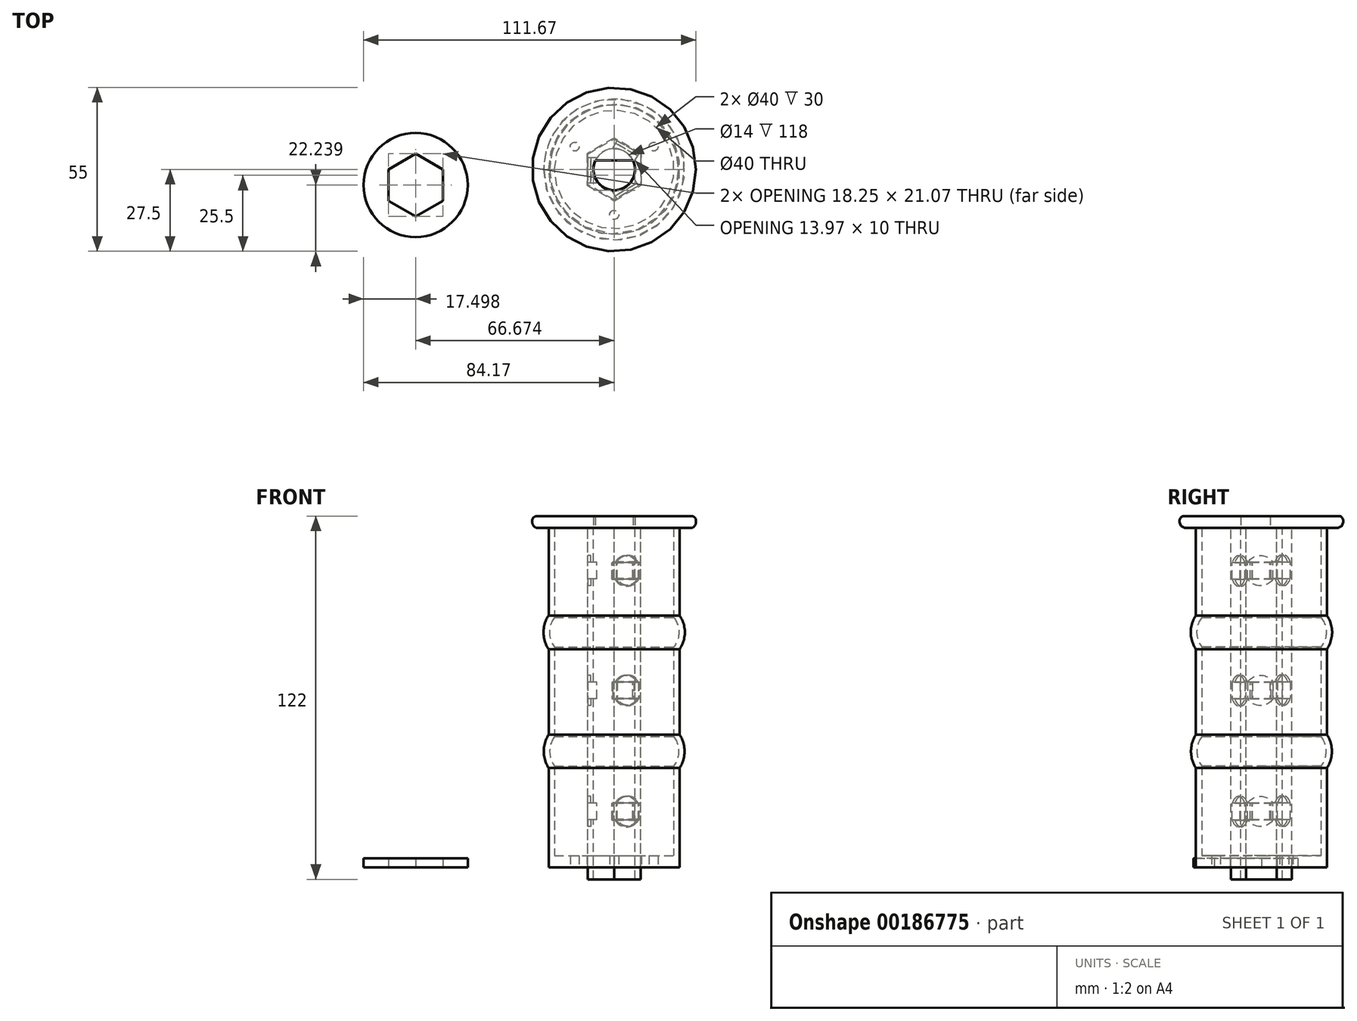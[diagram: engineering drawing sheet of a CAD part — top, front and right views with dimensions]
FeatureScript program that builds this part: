
annotation { "Feature Type Name" : "Feature", "Feature Type Description" : "" }
export const myFeature = defineFeature(function(context is Context, id is Id, definition is map)
    precondition{}
    {
        {
            var Q0;
            Q0=qCreatedBy(makeId("Front.planeOp"),FACE);
            var sketch = newSketch(context, id + "F0", { "sketchPlane" : qUnion([Q0])});
            skLineSegment(sketch, "E0.bottom", {"start": v(-20, 0) * mm, "end": v(20, 0) * mm});
            skLineSegment(sketch, "E0.top", {"start": v(-20, 4) * mm, "end": v(20, 4) * mm});
            skLineSegment(sketch, "E0.left", {"start": v(-20, 0) * mm, "end": v(-20, 4) * mm});
            skLineSegment(sketch, "E0.right", {"start": v(20, 0) * mm, "end": v(20, 4) * mm});
            skLineSegment(sketch, "E1.top", {"start": v(-20, 34) * mm, "end": v(20, 34) * mm});
            skLineSegment(sketch, "E1.left", {"start": v(-20, 4) * mm, "end": v(-20, 34) * mm});
            skLineSegment(sketch, "E1.right", {"start": v(20, 4) * mm, "end": v(20, 34) * mm});
            skLineSegment(sketch, "E2.top", {"start": v(-20, 44) * mm, "end": v(20, 44) * mm});
            skLineSegment(sketch, "E2.left", {"start": v(-20, 34) * mm, "end": v(-20, 44) * mm});
            skLineSegment(sketch, "E2.right", {"start": v(20, 34) * mm, "end": v(20, 44) * mm});
            skLineSegment(sketch, "E3", {"start": v(0, 0) * mm, "end": v(0, 48) * mm});
            skLineSegment(sketch, "E4.bottom", {"start": v(0, 0) * mm, "end": v(7, 0) * mm});
            skLineSegment(sketch, "E4.top", {"start": v(0, 4) * mm, "end": v(7, 4) * mm});
            skLineSegment(sketch, "E4.left", {"start": v(0, 0) * mm, "end": v(0, 4) * mm});
            skLineSegment(sketch, "E4.right", {"start": v(7, 0) * mm, "end": v(7, 4) * mm});
            skLineSegment(sketch, "E5.top", {"start": v(-20, 74) * mm, "end": v(20, 74) * mm});
            skLineSegment(sketch, "E5.left", {"start": v(-20, 44) * mm, "end": v(-20, 74) * mm});
            skLineSegment(sketch, "E5.right", {"start": v(20, 44) * mm, "end": v(20, 74) * mm});
            skLineSegment(sketch, "E6.top", {"start": v(-20, 84) * mm, "end": v(20, 84) * mm});
            skLineSegment(sketch, "E6.left", {"start": v(-20, 74) * mm, "end": v(-20, 84) * mm});
            skLineSegment(sketch, "E6.right", {"start": v(20, 74) * mm, "end": v(20, 84) * mm});
            skLineSegment(sketch, "E7.top", {"start": v(-20, 114) * mm, "end": v(20, 114) * mm});
            skLineSegment(sketch, "E7.left", {"start": v(-20, 84) * mm, "end": v(-20, 114) * mm});
            skLineSegment(sketch, "E7.right", {"start": v(20, 84) * mm, "end": v(20, 114) * mm});
            skPoint(sketch, "E8.third.point", {"position": v(0, 39) * mm});
            skPoint(sketch, "E8.third.point.positionSnap0", {"position": v(20, 39) * mm});
            skPoint(sketch, "E9.third.point", {"position": v(0, 79) * mm});
            skPoint(sketch, "E9.third.point.positionSnap0", {"position": v(20, 79) * mm});
            skArc(sketch, "E10", {"start": v(20, 34) * mm, "mid": v(21.65, 39) * mm, "end": v(20, 44) * mm});
            skArc(sketch, "E11", {"start": v(20, 74) * mm, "mid": v(21.75, 79) * mm, "end": v(20, 84) * mm});
            skLineSegment(sketch, "E12.0", {"start": v(22, 84.66) * mm, "end": v(22, 114) * mm});
            skArc(sketch, "E12.1", {"start": v(22, 73.34) * mm, "mid": v(23.75, 79) * mm, "end": v(22, 84.66) * mm});
            skLineSegment(sketch, "E12.2", {"start": v(22, 0) * mm, "end": v(22, 4) * mm});
            skLineSegment(sketch, "E12.3", {"start": v(22, 4) * mm, "end": v(22, 33.38) * mm});
            skArc(sketch, "E12.4", {"start": v(22, 33.38) * mm, "mid": v(23.65, 39) * mm, "end": v(22, 44.62) * mm});
            skLineSegment(sketch, "E12.5", {"start": v(22, 44.62) * mm, "end": v(22, 73.34) * mm});
            skLineSegment(sketch, "E13", {"start": v(20, 0) * mm, "end": v(22, 0) * mm});
            skLineSegment(sketch, "E14", {"start": v(20, 114) * mm, "end": v(22, 114) * mm});
            skPoint(sketch, "E15.visualSharp", {"position": v(22, 114) * mm});
            skLineSegment(sketch, "E15.filletArc", {"start": v(22, 114) * mm, "end": v(22, 114) * mm});
            skPoint(sketch, "E16.visualSharp", {"position": v(20, 114) * mm});
            skLineSegment(sketch, "E16.filletArc", {"start": v(20, 114) * mm, "end": v(20, 114) * mm});
            skSolve(sketch);
        }
        {
            var Q0;
            Q0=makeQuery(id+"F0.imprint","IMPRINT",FACE,{"disambiguationData":[TD([[makeQuery(id+"F0.imprint","IMPRINT",EDGE,{"derivedFrom":sQuery(id+"F0.wireOp",EDGE,"E0.right")}),-1.0]])]});
            var Q1;
            {var subQ0=sQuery(id+"F0.wireOp",EDGE,"E0.right");Q1=makeQuery(id+"F0.imprint","IMPRINT",FACE,{"disambiguationData":[TD([[makeQuery(id+"F0.imprint","IMPRINT",EDGE,{"derivedFrom":subQ0}),1.0]])]});}
            var Q2;
            Q2=sQuery(id+"F0.wireOp",EDGE,"E3");
            revolve(context, id + "F1", {"entities" : qUnion([Q0, Q1]), "axis" : qUnion([Q2]), "revolveType" : RevolveType.FULL});
        }
        {
            var Q0;
            Q0=makeQuery(id+"F1.opRevolve","SWEPT_FACE",FACE,{"disambiguationData":[OSD([sQuery(id+"F0.wireOp",EDGE,"E0.bottom"),sQuery(id+"F0.wireOp",EDGE,"E13")])]});
            var sketch = newSketch(context, id + "F2", { "sketchPlane" : qUnion([Q0])});
            skCircle(sketch, "E17.cCircle", {"center": v(0, 0) * mm, "radius": 13.23 * mm, "construction": true});
            skLineSegment(sketch, "E17.0", {"start": v(0, 15.28) * mm, "end": v(13.23, 7.64) * mm});
            skLineSegment(sketch, "E17.1", {"start": v(13.23, 7.64) * mm, "end": v(13.23, -7.64) * mm});
            skLineSegment(sketch, "E17.2", {"start": v(13.23, -7.64) * mm, "end": v(0, -15.28) * mm});
            skLineSegment(sketch, "E17.3", {"start": v(0, -15.28) * mm, "end": v(-13.23, -7.64) * mm});
            skLineSegment(sketch, "E17.4", {"start": v(-13.23, -7.64) * mm, "end": v(-13.23, 7.64) * mm});
            skLineSegment(sketch, "E17.5", {"start": v(-13.23, 7.64) * mm, "end": v(0, 15.28) * mm});
            skPoint(sketch, "E17.0.midPoint", {"position": v(6.61, 11.46) * mm});
            skCircle(sketch, "E18", {"center": v(0, 15.28) * mm, "radius": 1.5 * mm});
            skCircle(sketch, "E19", {"center": v(-13.23, -7.64) * mm, "radius": 1.5 * mm});
            skCircle(sketch, "E20", {"center": v(13.23, -7.64) * mm, "radius": 1.5 * mm});
            skCircle(sketch, "E21.cCircle", {"center": v(0, 0) * mm, "radius": 8.88 * mm, "construction": true});
            skLineSegment(sketch, "E21.0", {"start": v(8.88, 5.12) * mm, "end": v(8.88, -5.12) * mm});
            skLineSegment(sketch, "E21.1", {"start": v(8.88, -5.12) * mm, "end": v(0, -10.25) * mm});
            skLineSegment(sketch, "E21.2", {"start": v(0, -10.25) * mm, "end": v(-8.87, -5.12) * mm});
            skLineSegment(sketch, "E21.3", {"start": v(-8.87, -5.12) * mm, "end": v(-8.87, 5.12) * mm});
            skLineSegment(sketch, "E21.4", {"start": v(-8.87, 5.12) * mm, "end": v(0, 10.25) * mm});
            skLineSegment(sketch, "E21.5", {"start": v(0, 10.25) * mm, "end": v(8.88, 5.12) * mm});
            skPoint(sketch, "E21.0.midPoint", {"position": v(8.88, 0) * mm});
            skCircle(sketch, "E22", {"center": v(0, 0) * mm, "radius": 7 * mm});
            skCircle(sketch, "E23.cCircle", {"center": v(0, 0) * mm, "radius": 8.47 * mm, "construction": true});
            skLineSegment(sketch, "E23.0", {"start": v(0, 9.78) * mm, "end": v(8.47, 4.89) * mm});
            skLineSegment(sketch, "E23.1", {"start": v(8.47, 4.89) * mm, "end": v(8.47, -4.89) * mm});
            skLineSegment(sketch, "E23.2", {"start": v(8.47, -4.89) * mm, "end": v(0, -9.78) * mm});
            skLineSegment(sketch, "E23.3", {"start": v(0, -9.78) * mm, "end": v(-8.47, -4.89) * mm});
            skLineSegment(sketch, "E23.4", {"start": v(-8.47, -4.89) * mm, "end": v(-8.47, 4.89) * mm});
            skLineSegment(sketch, "E23.5", {"start": v(-8.47, 4.89) * mm, "end": v(0, 9.78) * mm});
            skPoint(sketch, "E23.0.midPoint", {"position": v(4.24, 7.33) * mm});
            skCircle(sketch, "E24.cCircle", {"center": v(0, 0) * mm, "radius": 9.12 * mm, "construction": true});
            skLineSegment(sketch, "E24.0", {"start": v(0, 10.54) * mm, "end": v(9.13, 5.27) * mm});
            skLineSegment(sketch, "E24.1", {"start": v(9.13, 5.27) * mm, "end": v(9.13, -5.27) * mm});
            skLineSegment(sketch, "E24.2", {"start": v(9.13, -5.27) * mm, "end": v(0, -10.54) * mm});
            skLineSegment(sketch, "E24.3", {"start": v(0, -10.54) * mm, "end": v(-9.12, -5.27) * mm});
            skLineSegment(sketch, "E24.4", {"start": v(-9.12, -5.27) * mm, "end": v(-9.12, 5.27) * mm});
            skLineSegment(sketch, "E24.5", {"start": v(-9.12, 5.27) * mm, "end": v(0, 10.54) * mm});
            skPoint(sketch, "E24.0.midPoint", {"position": v(4.57, 7.9) * mm});
            skSolve(sketch);
        }
        {
            var Q0;
            {var subQ0=sQuery(id+"F2.wireOp",EDGE,"E17.5");var subQ1=sQuery(id+"F2.wireOp",EDGE,"E17.0");var subQ2=makeQuery(id+"F2.imprint","INTERSECT",VERTEX,{"derivedFrom":[subQ1,subQ0]});Q0=makeQuery(id+"F2.imprint","IMPRINT",FACE,{"disambiguationData":[TD([[makeQuery(id+"F2.imprint","IMPRINT",EDGE,{"disambiguationData":[TD([[subQ2,-1.0]])],"derivedFrom":subQ1}),-1.0]])]});}
            var Q1;
            {var subQ0=sQuery(id+"F2.wireOp",EDGE,"E17.5");var subQ1=sQuery(id+"F2.wireOp",EDGE,"E17.0");var subQ2=makeQuery(id+"F2.imprint","INTERSECT",VERTEX,{"derivedFrom":[subQ1,subQ0]});Q1=makeQuery(id+"F2.imprint","IMPRINT",FACE,{"disambiguationData":[TD([[makeQuery(id+"F2.imprint","IMPRINT",EDGE,{"disambiguationData":[TD([[subQ2,-1.0]])],"derivedFrom":subQ1}),1.0]])]});}
            var Q2;
            {var subQ0=sQuery(id+"F2.wireOp",EDGE,"E17.2");var subQ1=sQuery(id+"F2.wireOp",EDGE,"E17.1");var subQ2=makeQuery(id+"F2.imprint","INTERSECT",VERTEX,{"derivedFrom":[subQ1,subQ0]});Q2=makeQuery(id+"F2.imprint","IMPRINT",FACE,{"disambiguationData":[TD([[makeQuery(id+"F2.imprint","IMPRINT",EDGE,{"disambiguationData":[TD([[subQ2,1.0]])],"derivedFrom":subQ1}),1.0]])]});}
            var Q3;
            {var subQ0=sQuery(id+"F2.wireOp",EDGE,"E17.2");var subQ1=sQuery(id+"F2.wireOp",EDGE,"E17.1");var subQ2=makeQuery(id+"F2.imprint","INTERSECT",VERTEX,{"derivedFrom":[subQ1,subQ0]});Q3=makeQuery(id+"F2.imprint","IMPRINT",FACE,{"disambiguationData":[TD([[makeQuery(id+"F2.imprint","IMPRINT",EDGE,{"disambiguationData":[TD([[subQ2,1.0]])],"derivedFrom":subQ1}),-1.0]])]});}
            var Q4;
            {var subQ0=sQuery(id+"F2.wireOp",EDGE,"E17.4");var subQ1=sQuery(id+"F2.wireOp",EDGE,"E17.3");var subQ2=makeQuery(id+"F2.imprint","INTERSECT",VERTEX,{"derivedFrom":[subQ1,subQ0]});Q4=makeQuery(id+"F2.imprint","IMPRINT",FACE,{"disambiguationData":[TD([[makeQuery(id+"F2.imprint","IMPRINT",EDGE,{"disambiguationData":[TD([[subQ2,1.0]])],"derivedFrom":subQ1}),-1.0]])]});}
            var Q5;
            {var subQ0=sQuery(id+"F2.wireOp",EDGE,"E17.4");var subQ1=sQuery(id+"F2.wireOp",EDGE,"E17.3");var subQ2=makeQuery(id+"F2.imprint","INTERSECT",VERTEX,{"derivedFrom":[subQ1,subQ0]});Q5=makeQuery(id+"F2.imprint","IMPRINT",FACE,{"disambiguationData":[TD([[makeQuery(id+"F2.imprint","IMPRINT",EDGE,{"disambiguationData":[TD([[subQ2,1.0]])],"derivedFrom":subQ1}),1.0]])]});}
            var Q6;
            Q6=makeQuery(id+"F2.imprint","IMPRINT",FACE,{"disambiguationData":[TD([[makeQuery(id+"F2.imprint","IMPRINT",EDGE,{"derivedFrom":sQuery(id+"F2.wireOp",EDGE,"E23.0")}),-1.0]])]});
            var Q7;
            Q7=makeQuery(id+"F2.imprint","IMPRINT",FACE,{"disambiguationData":[TD([[makeQuery(id+"F2.imprint","IMPRINT",EDGE,{"derivedFrom":sQuery(id+"F2.wireOp",EDGE,"E21.0")}),-1.0]])]});
            var Q8;
            Q8=makeQuery(id+"F2.imprint","IMPRINT",FACE,{"disambiguationData":[TD([[makeQuery(id+"F2.imprint","IMPRINT",EDGE,{"derivedFrom":sQuery(id+"F2.wireOp",EDGE,"E21.0")}),1.0]])]});
            extrude(context, id + "F3", {"entities" : qUnion([Q0, Q1, Q2, Q3, Q4, Q5, Q6, Q7, Q8]), "operationType" : NewBodyOperationType.REMOVE, "oppositeDirection" : true, "depth" : 4 * mm});
        }
        {
            var Q0;
            Q0=makeQuery(id+"F1.opRevolve","SWEPT_FACE",FACE,{"disambiguationData":[OSD([sQuery(id+"F0.wireOp",EDGE,"E14")])]});
            var sketch = newSketch(context, id + "F4", { "sketchPlane" : qUnion([Q0])});
            skCircle(sketch, "E25.cCircle", {"center": v(0, 0) * mm, "radius": 8.88 * mm, "construction": true});
            skLineSegment(sketch, "E25.0", {"start": v(8.88, 5.12) * mm, "end": v(8.88, -5.12) * mm});
            skLineSegment(sketch, "E25.1", {"start": v(8.88, -5.12) * mm, "end": v(0, -10.25) * mm});
            skLineSegment(sketch, "E25.2", {"start": v(0, -10.25) * mm, "end": v(-8.88, -5.12) * mm});
            skLineSegment(sketch, "E25.3", {"start": v(-8.88, -5.12) * mm, "end": v(-8.88, 5.12) * mm});
            skLineSegment(sketch, "E25.4", {"start": v(-8.88, 5.12) * mm, "end": v(0, 10.25) * mm});
            skLineSegment(sketch, "E25.5", {"start": v(0, 10.25) * mm, "end": v(8.88, 5.12) * mm});
            skPoint(sketch, "E25.0.midPoint", {"position": v(8.88, 0) * mm});
            skCircle(sketch, "E26", {"center": v(0, 0) * mm, "radius": 7 * mm});
            skCircle(sketch, "E27", {"center": v(0, 0) * mm, "radius": 27.5 * mm});
            skLineSegment(sketch, "E28", {"start": v(0, 3) * mm, "end": v(6.32, 3) * mm});
            skLineSegment(sketch, "E29", {"start": v(0, 3) * mm, "end": v(-6.32, 3) * mm});
            skSolve(sketch);
        }
        {
            var Q0;
            Q0=makeQuery(id+"F4.imprint","IMPRINT",FACE,{"disambiguationData":[TD([[makeQuery(id+"F4.imprint","IMPRINT",EDGE,{"derivedFrom":sQuery(id+"F4.wireOp",EDGE,"E25.0")}),-1.0]])]});
            extrude(context, id + "F5", {"entities" : qUnion([Q0]), "oppositeDirection" : true, "depth" : 118 * mm});
        }
        {
            var Q0;
            Q0=makeQuery(id+"F4.imprint","IMPRINT",FACE,{"disambiguationData":[TD([[makeQuery(id+"F4.imprint","IMPRINT",EDGE,{"derivedFrom":sQuery(id+"F4.wireOp",EDGE,"E27")}),1.0]])]});
            var Q1;
            {var subQ0=sQuery(id+"F0.wireOp",EDGE,"E14");Q1=makeQuery(id+"F4.imprint","IMPRINT",FACE,{"disambiguationData":[TD([[makeQuery(id+"F4.imprint","IMPRINT",EDGE,{"derivedFrom":makeQuery(id+"F1.opRevolve","SWEPT_EDGE",EDGE,{"disambiguationData":[OSD([subQ0,sQuery(id+"F0.wireOp",EDGE,"E16.filletArc")])]})}),1.0]])]});}
            var Q2;
            Q2=makeQuery(id+"F4.imprint","IMPRINT",FACE,{"disambiguationData":[TD([[makeQuery(id+"F4.imprint","IMPRINT",EDGE,{"derivedFrom":sQuery(id+"F4.wireOp",EDGE,"E25.0")}),1.0]])]});
            var Q3;
            Q3=makeQuery(id+"F4.imprint","IMPRINT",FACE,{"disambiguationData":[TD([[makeQuery(id+"F4.imprint","IMPRINT",EDGE,{"derivedFrom":sQuery(id+"F4.wireOp",EDGE,"E25.0")}),-1.0]])]});
            var Q4;
            {var subQ0=sQuery(id+"F0.wireOp",EDGE,"E14");Q4=makeQuery(id+"F4.imprint","IMPRINT",FACE,{"disambiguationData":[TD([[makeQuery(id+"F4.imprint","IMPRINT",EDGE,{"derivedFrom":makeQuery(id+"F1.opRevolve","SWEPT_EDGE",EDGE,{"disambiguationData":[OSD([sQuery(id+"F0.wireOp",EDGE,"E12.0"),subQ0])]})}),-1.0]])]});}
            var Q5;
            {var subQ0=sQuery(id+"F4.wireOp",EDGE,"E28");Q5=makeQuery(id+"F4.imprint","IMPRINT",FACE,{"disambiguationData":[TD([[makeQuery(id+"F4.imprint","IMPRINT",EDGE,{"derivedFrom":subQ0}),1.0]])]});}
            extrude(context, id + "F6", {"entities" : qUnion([Q0, Q1, Q2, Q3, Q4, Q5]), "depth" : 4 * mm});
        }
        {
            var Q0;
            Q0=makeQuery(id+"F6.opExtrude","CAP_EDGE",EDGE,{"disambiguationData":[OSD([sQuery(id+"F4.wireOp",EDGE,"E27")])],"isStart":true});
            fillet(context, id + "F7", {"entities" : qUnion([Q0]), "radius" : 2 * mm, "tangentPropagation" : true, "allowEdgeOverflow" : false});
        }
        {
            var Q0;
            Q0=makeQuery(id+"F5.opExtrude","SWEPT_FACE",FACE,{"disambiguationData":[OSD([sQuery(id+"F4.wireOp",EDGE,"E25.1")])]});
            var sketch = newSketch(context, id + "F8", { "sketchPlane" : qUnion([Q0])});
            skCircle(sketch, "E30", {"center": v(0, 59.42) * mm, "radius": 5.1 * mm});
            skPoint(sketch, "E30.centerSnap0", {"position": v(0, 114) * mm});
            skCircle(sketch, "E31", {"center": v(0, 99.62) * mm, "radius": 5.1 * mm});
            skCircle(sketch, "E32", {"center": v(0, 18.73) * mm, "radius": 5.1 * mm});
            skLineSegment(sketch, "E33.bottom", {"start": v(-4.25, 62.24) * mm, "end": v(4.25, 62.24) * mm});
            skLineSegment(sketch, "E33.top", {"start": v(-4.25, 56.6) * mm, "end": v(4.25, 56.6) * mm});
            skLineSegment(sketch, "E33.left", {"start": v(-4.25, 62.24) * mm, "end": v(-4.25, 56.6) * mm});
            skLineSegment(sketch, "E33.right", {"start": v(4.25, 62.24) * mm, "end": v(4.25, 56.6) * mm});
            skLineSegment(sketch, "E34.bottom", {"start": v(-4.25, 96.8) * mm, "end": v(4.25, 96.8) * mm});
            skLineSegment(sketch, "E34.top", {"start": v(-4.25, 102.44) * mm, "end": v(4.25, 102.44) * mm});
            skLineSegment(sketch, "E34.left", {"start": v(-4.25, 96.8) * mm, "end": v(-4.25, 102.44) * mm});
            skLineSegment(sketch, "E34.right", {"start": v(4.25, 96.8) * mm, "end": v(4.25, 102.44) * mm});
            skLineSegment(sketch, "E35.bottom", {"start": v(-4.25, 15.91) * mm, "end": v(4.25, 15.91) * mm});
            skLineSegment(sketch, "E35.top", {"start": v(-4.25, 21.55) * mm, "end": v(4.25, 21.55) * mm});
            skLineSegment(sketch, "E35.left", {"start": v(-4.25, 15.91) * mm, "end": v(-4.25, 21.55) * mm});
            skLineSegment(sketch, "E35.right", {"start": v(4.25, 15.91) * mm, "end": v(4.25, 21.55) * mm});
            skSolve(sketch);
        }
        {
            var Q0;
            {var subQ0=sQuery(id+"F8.wireOp",EDGE,"E33.bottom");Q0=makeQuery(id+"F8.imprint","IMPRINT",FACE,{"disambiguationData":[TD([[makeQuery(id+"F8.imprint","IMPRINT",EDGE,{"derivedFrom":subQ0}),1.0]])]});}
            var Q1;
            {var subQ0=sQuery(id+"F8.wireOp",EDGE,"E33.top");Q1=makeQuery(id+"F8.imprint","IMPRINT",FACE,{"disambiguationData":[TD([[makeQuery(id+"F8.imprint","IMPRINT",EDGE,{"derivedFrom":subQ0}),-1.0]])]});}
            var Q2;
            {var subQ0=sQuery(id+"F8.wireOp",EDGE,"E34.top");Q2=makeQuery(id+"F8.imprint","IMPRINT",FACE,{"disambiguationData":[TD([[makeQuery(id+"F8.imprint","IMPRINT",EDGE,{"derivedFrom":subQ0}),1.0]])]});}
            var Q3;
            {var subQ0=sQuery(id+"F8.wireOp",EDGE,"E34.bottom");Q3=makeQuery(id+"F8.imprint","IMPRINT",FACE,{"disambiguationData":[TD([[makeQuery(id+"F8.imprint","IMPRINT",EDGE,{"derivedFrom":subQ0}),-1.0]])]});}
            var Q4;
            {var subQ0=sQuery(id+"F8.wireOp",EDGE,"E35.top");Q4=makeQuery(id+"F8.imprint","IMPRINT",FACE,{"disambiguationData":[TD([[makeQuery(id+"F8.imprint","IMPRINT",EDGE,{"derivedFrom":subQ0}),1.0]])]});}
            var Q5;
            {var subQ0=sQuery(id+"F8.wireOp",EDGE,"E35.bottom");Q5=makeQuery(id+"F8.imprint","IMPRINT",FACE,{"disambiguationData":[TD([[makeQuery(id+"F8.imprint","IMPRINT",EDGE,{"derivedFrom":subQ0}),-1.0]])]});}
            var Q6;
            Q6=makeQuery(id+"F8.imprint","IMPRINT",FACE,{"disambiguationData":[TD([[makeQuery(id+"F8.imprint","IMPRINT",EDGE,{"derivedFrom":sQuery(id+"F8.wireOp",EDGE,"E33.bottom")}),-1.0]])]});
            var Q7;
            Q7=makeQuery(id+"F8.imprint","IMPRINT",FACE,{"disambiguationData":[TD([[makeQuery(id+"F8.imprint","IMPRINT",EDGE,{"derivedFrom":sQuery(id+"F8.wireOp",EDGE,"E34.bottom")}),1.0]])]});
            var Q8;
            Q8=makeQuery(id+"F8.imprint","IMPRINT",FACE,{"disambiguationData":[TD([[makeQuery(id+"F8.imprint","IMPRINT",EDGE,{"derivedFrom":sQuery(id+"F8.wireOp",EDGE,"E35.bottom")}),1.0]])]});
            extrude(context, id + "F9", {"entities" : qUnion([Q0, Q1, Q2, Q3, Q4, Q5, Q6, Q7, Q8]), "operationType" : NewBodyOperationType.REMOVE, "oppositeDirection" : true, "depth" : 1 * mm});
        }
        {
            var Q0;
            Q0=makeQuery(id+"F5.opExtrude","SWEPT_FACE",FACE,{"disambiguationData":[OSD([sQuery(id+"F4.wireOp",EDGE,"E25.3")])]});
            var sketch = newSketch(context, id + "F10", { "sketchPlane" : qUnion([Q0])});
            skCircle(sketch, "E36", {"center": v(0.35, 59.49) * mm, "radius": 5.1 * mm});
            skPoint(sketch, "E36.centerSnap0", {"position": v(0.35, 114.07) * mm});
            skCircle(sketch, "E37", {"center": v(0.35, 99.69) * mm, "radius": 5.1 * mm});
            skCircle(sketch, "E38", {"center": v(0.35, 18.8) * mm, "radius": 5.1 * mm});
            skLineSegment(sketch, "E39.bottom", {"start": v(-3.9, 62.3) * mm, "end": v(4.6, 62.3) * mm});
            skLineSegment(sketch, "E39.top", {"start": v(-3.9, 56.67) * mm, "end": v(4.6, 56.67) * mm});
            skLineSegment(sketch, "E39.left", {"start": v(-3.9, 62.3) * mm, "end": v(-3.9, 56.67) * mm});
            skLineSegment(sketch, "E39.right", {"start": v(4.6, 62.3) * mm, "end": v(4.6, 56.67) * mm});
            skLineSegment(sketch, "E40.bottom", {"start": v(-3.9, 96.87) * mm, "end": v(4.6, 96.87) * mm});
            skLineSegment(sketch, "E40.top", {"start": v(-3.9, 102.5) * mm, "end": v(4.6, 102.5) * mm});
            skLineSegment(sketch, "E40.left", {"start": v(-3.9, 96.87) * mm, "end": v(-3.9, 102.5) * mm});
            skLineSegment(sketch, "E40.right", {"start": v(4.6, 96.87) * mm, "end": v(4.6, 102.5) * mm});
            skLineSegment(sketch, "E41.bottom", {"start": v(-3.9, 15.98) * mm, "end": v(4.6, 15.98) * mm});
            skLineSegment(sketch, "E41.top", {"start": v(-3.9, 21.62) * mm, "end": v(4.6, 21.62) * mm});
            skLineSegment(sketch, "E41.left", {"start": v(-3.9, 15.98) * mm, "end": v(-3.9, 21.62) * mm});
            skLineSegment(sketch, "E41.right", {"start": v(4.6, 15.98) * mm, "end": v(4.6, 21.62) * mm});
            skSolve(sketch);
        }
        {
            var Q0;
            Q0=makeQuery(id+"F5.opExtrude","SWEPT_FACE",FACE,{"disambiguationData":[OSD([sQuery(id+"F4.wireOp",EDGE,"E25.5")])]});
            var sketch = newSketch(context, id + "F11", { "sketchPlane" : qUnion([Q0])});
            skCircle(sketch, "E42", {"center": v(-0.26, 59.6) * mm, "radius": 5.1 * mm});
            skPoint(sketch, "E42.centerSnap0", {"position": v(-0.26, 114.19) * mm});
            skCircle(sketch, "E43", {"center": v(-0.26, 99.8) * mm, "radius": 5.1 * mm});
            skCircle(sketch, "E44", {"center": v(-0.26, 18.92) * mm, "radius": 5.1 * mm});
            skLineSegment(sketch, "E45.bottom", {"start": v(-4.51, 62.42) * mm, "end": v(3.99, 62.42) * mm});
            skLineSegment(sketch, "E45.top", {"start": v(-4.51, 56.79) * mm, "end": v(3.99, 56.79) * mm});
            skLineSegment(sketch, "E45.left", {"start": v(-4.51, 62.42) * mm, "end": v(-4.51, 56.79) * mm});
            skLineSegment(sketch, "E45.right", {"start": v(3.99, 62.42) * mm, "end": v(3.99, 56.79) * mm});
            skLineSegment(sketch, "E46.bottom", {"start": v(-4.51, 96.99) * mm, "end": v(3.99, 96.99) * mm});
            skLineSegment(sketch, "E46.top", {"start": v(-4.51, 102.63) * mm, "end": v(3.99, 102.63) * mm});
            skLineSegment(sketch, "E46.left", {"start": v(-4.51, 96.99) * mm, "end": v(-4.51, 102.63) * mm});
            skLineSegment(sketch, "E46.right", {"start": v(3.99, 96.99) * mm, "end": v(3.99, 102.63) * mm});
            skLineSegment(sketch, "E47.bottom", {"start": v(-4.51, 16.1) * mm, "end": v(3.99, 16.1) * mm});
            skLineSegment(sketch, "E47.top", {"start": v(-4.51, 21.74) * mm, "end": v(3.99, 21.74) * mm});
            skLineSegment(sketch, "E47.left", {"start": v(-4.51, 16.1) * mm, "end": v(-4.51, 21.74) * mm});
            skLineSegment(sketch, "E47.right", {"start": v(3.99, 16.1) * mm, "end": v(3.99, 21.74) * mm});
            skSolve(sketch);
        }
        {
            var Q0;
            Q0=makeQuery(id+"F11.imprint","IMPRINT",FACE,{"disambiguationData":[TD([[makeQuery(id+"F11.imprint","IMPRINT",EDGE,{"derivedFrom":sQuery(id+"F11.wireOp",EDGE,"E45.bottom")}),-1.0]])]});
            var Q1;
            {var subQ0=sQuery(id+"F11.wireOp",EDGE,"E45.bottom");Q1=makeQuery(id+"F11.imprint","IMPRINT",FACE,{"disambiguationData":[TD([[makeQuery(id+"F11.imprint","IMPRINT",EDGE,{"derivedFrom":subQ0}),1.0]])]});}
            var Q2;
            {var subQ0=sQuery(id+"F11.wireOp",EDGE,"E45.top");Q2=makeQuery(id+"F11.imprint","IMPRINT",FACE,{"disambiguationData":[TD([[makeQuery(id+"F11.imprint","IMPRINT",EDGE,{"derivedFrom":subQ0}),-1.0]])]});}
            var Q3;
            Q3=makeQuery(id+"F11.imprint","IMPRINT",FACE,{"disambiguationData":[TD([[makeQuery(id+"F11.imprint","IMPRINT",EDGE,{"derivedFrom":sQuery(id+"F11.wireOp",EDGE,"E46.bottom")}),1.0]])]});
            var Q4;
            {var subQ0=sQuery(id+"F11.wireOp",EDGE,"E46.top");Q4=makeQuery(id+"F11.imprint","IMPRINT",FACE,{"disambiguationData":[TD([[makeQuery(id+"F11.imprint","IMPRINT",EDGE,{"derivedFrom":subQ0}),1.0]])]});}
            var Q5;
            {var subQ0=sQuery(id+"F11.wireOp",EDGE,"E46.bottom");Q5=makeQuery(id+"F11.imprint","IMPRINT",FACE,{"disambiguationData":[TD([[makeQuery(id+"F11.imprint","IMPRINT",EDGE,{"derivedFrom":subQ0}),-1.0]])]});}
            var Q6;
            {var subQ0=sQuery(id+"F11.wireOp",EDGE,"E47.top");Q6=makeQuery(id+"F11.imprint","IMPRINT",FACE,{"disambiguationData":[TD([[makeQuery(id+"F11.imprint","IMPRINT",EDGE,{"derivedFrom":subQ0}),1.0]])]});}
            var Q7;
            Q7=makeQuery(id+"F11.imprint","IMPRINT",FACE,{"disambiguationData":[TD([[makeQuery(id+"F11.imprint","IMPRINT",EDGE,{"derivedFrom":sQuery(id+"F11.wireOp",EDGE,"E47.bottom")}),1.0]])]});
            var Q8;
            {var subQ0=sQuery(id+"F11.wireOp",EDGE,"E47.bottom");Q8=makeQuery(id+"F11.imprint","IMPRINT",FACE,{"disambiguationData":[TD([[makeQuery(id+"F11.imprint","IMPRINT",EDGE,{"derivedFrom":subQ0}),-1.0]])]});}
            extrude(context, id + "F12", {"entities" : qUnion([Q0, Q1, Q2, Q3, Q4, Q5, Q6, Q7, Q8]), "operationType" : NewBodyOperationType.REMOVE, "oppositeDirection" : true, "depth" : 1 * mm});
        }
        {
            var Q0;
            {var subQ0=sQuery(id+"F10.wireOp",EDGE,"E39.top");Q0=makeQuery(id+"F10.imprint","IMPRINT",FACE,{"disambiguationData":[TD([[makeQuery(id+"F10.imprint","IMPRINT",EDGE,{"derivedFrom":subQ0}),-1.0]])]});}
            var Q1;
            Q1=makeQuery(id+"F10.imprint","IMPRINT",FACE,{"disambiguationData":[TD([[makeQuery(id+"F10.imprint","IMPRINT",EDGE,{"derivedFrom":sQuery(id+"F10.wireOp",EDGE,"E39.bottom")}),-1.0]])]});
            var Q2;
            {var subQ0=sQuery(id+"F10.wireOp",EDGE,"E39.bottom");Q2=makeQuery(id+"F10.imprint","IMPRINT",FACE,{"disambiguationData":[TD([[makeQuery(id+"F10.imprint","IMPRINT",EDGE,{"derivedFrom":subQ0}),1.0]])]});}
            var Q3;
            {var subQ0=sQuery(id+"F10.wireOp",EDGE,"E41.top");Q3=makeQuery(id+"F10.imprint","IMPRINT",FACE,{"disambiguationData":[TD([[makeQuery(id+"F10.imprint","IMPRINT",EDGE,{"derivedFrom":subQ0}),1.0]])]});}
            var Q4;
            Q4=makeQuery(id+"F10.imprint","IMPRINT",FACE,{"disambiguationData":[TD([[makeQuery(id+"F10.imprint","IMPRINT",EDGE,{"derivedFrom":sQuery(id+"F10.wireOp",EDGE,"E41.bottom")}),1.0]])]});
            var Q5;
            {var subQ0=sQuery(id+"F10.wireOp",EDGE,"E41.bottom");Q5=makeQuery(id+"F10.imprint","IMPRINT",FACE,{"disambiguationData":[TD([[makeQuery(id+"F10.imprint","IMPRINT",EDGE,{"derivedFrom":subQ0}),-1.0]])]});}
            var Q6;
            {var subQ0=sQuery(id+"F10.wireOp",EDGE,"E40.bottom");Q6=makeQuery(id+"F10.imprint","IMPRINT",FACE,{"disambiguationData":[TD([[makeQuery(id+"F10.imprint","IMPRINT",EDGE,{"derivedFrom":subQ0}),-1.0]])]});}
            var Q7;
            Q7=makeQuery(id+"F10.imprint","IMPRINT",FACE,{"disambiguationData":[TD([[makeQuery(id+"F10.imprint","IMPRINT",EDGE,{"derivedFrom":sQuery(id+"F10.wireOp",EDGE,"E40.bottom")}),1.0]])]});
            var Q8;
            {var subQ0=sQuery(id+"F10.wireOp",EDGE,"E40.top");Q8=makeQuery(id+"F10.imprint","IMPRINT",FACE,{"disambiguationData":[TD([[makeQuery(id+"F10.imprint","IMPRINT",EDGE,{"derivedFrom":subQ0}),1.0]])]});}
            extrude(context, id + "F13", {"entities" : qUnion([Q0, Q1, Q2, Q3, Q4, Q5, Q6, Q7, Q8]), "operationType" : NewBodyOperationType.REMOVE, "oppositeDirection" : true, "depth" : 1 * mm});
        }
        {
            var Q0;
            Q0=makeQuery(id+"F8.imprint","IMPRINT",FACE,{"disambiguationData":[TD([[makeQuery(id+"F8.imprint","IMPRINT",EDGE,{"derivedFrom":sQuery(id+"F8.wireOp",EDGE,"E33.bottom")}),-1.0]])]});
            var Q1;
            Q1=makeQuery(id+"F8.imprint","IMPRINT",FACE,{"disambiguationData":[TD([[makeQuery(id+"F8.imprint","IMPRINT",EDGE,{"derivedFrom":sQuery(id+"F8.wireOp",EDGE,"E34.bottom")}),1.0]])]});
            var Q2;
            Q2=makeQuery(id+"F8.imprint","IMPRINT",FACE,{"disambiguationData":[TD([[makeQuery(id+"F8.imprint","IMPRINT",EDGE,{"derivedFrom":sQuery(id+"F8.wireOp",EDGE,"E35.bottom")}),1.0]])]});
            extrude(context, id + "F14", {"entities" : qUnion([Q0, Q1, Q2]), "operationType" : NewBodyOperationType.REMOVE, "oppositeDirection" : true, "depth" : 3 * mm});
        }
        {
            var Q0;
            Q0=makeQuery(id+"F11.imprint","IMPRINT",FACE,{"disambiguationData":[TD([[makeQuery(id+"F11.imprint","IMPRINT",EDGE,{"derivedFrom":sQuery(id+"F11.wireOp",EDGE,"E45.bottom")}),-1.0]])]});
            var Q1;
            Q1=makeQuery(id+"F11.imprint","IMPRINT",FACE,{"disambiguationData":[TD([[makeQuery(id+"F11.imprint","IMPRINT",EDGE,{"derivedFrom":sQuery(id+"F11.wireOp",EDGE,"E46.bottom")}),1.0]])]});
            var Q2;
            Q2=makeQuery(id+"F11.imprint","IMPRINT",FACE,{"disambiguationData":[TD([[makeQuery(id+"F11.imprint","IMPRINT",EDGE,{"derivedFrom":sQuery(id+"F11.wireOp",EDGE,"E47.bottom")}),1.0]])]});
            extrude(context, id + "F15", {"entities" : qUnion([Q0, Q1, Q2]), "operationType" : NewBodyOperationType.REMOVE, "oppositeDirection" : true, "depth" : 3 * mm});
        }
        {
            var Q0;
            Q0=makeQuery(id+"F10.imprint","IMPRINT",FACE,{"disambiguationData":[TD([[makeQuery(id+"F10.imprint","IMPRINT",EDGE,{"derivedFrom":sQuery(id+"F10.wireOp",EDGE,"E40.bottom")}),1.0]])]});
            var Q1;
            Q1=makeQuery(id+"F10.imprint","IMPRINT",FACE,{"disambiguationData":[TD([[makeQuery(id+"F10.imprint","IMPRINT",EDGE,{"derivedFrom":sQuery(id+"F10.wireOp",EDGE,"E39.bottom")}),-1.0]])]});
            var Q2;
            Q2=makeQuery(id+"F10.imprint","IMPRINT",FACE,{"disambiguationData":[TD([[makeQuery(id+"F10.imprint","IMPRINT",EDGE,{"derivedFrom":sQuery(id+"F10.wireOp",EDGE,"E41.bottom")}),1.0]])]});
            extrude(context, id + "F16", {"entities" : qUnion([Q0, Q1, Q2]), "operationType" : NewBodyOperationType.REMOVE, "oppositeDirection" : true, "depth" : 3 * mm});
        }
        {
            var Q0;
            Q0=makeQuery(id+"F6.opExtrude","CAP_EDGE",EDGE,{"disambiguationData":[OSD([sQuery(id+"F4.wireOp",EDGE,"E27")])],"isStart":false});
            fillet(context, id + "F17", {"entities" : qUnion([Q0]), "radius" : 1.5 * mm, "tangentPropagation" : true, "allowEdgeOverflow" : false});
        }
        {
            var Q0;
            Q0=qCreatedBy(makeId("Top.planeOp"),FACE);
            var sketch = newSketch(context, id + "F18", { "sketchPlane" : qUnion([Q0])});
            skCircle(sketch, "E48.cCircle", {"center": v(-66.67, -5.26) * mm, "radius": 13.23 * mm, "construction": true});
            skLineSegment(sketch, "E48.0", {"start": v(-66.67, 10.01) * mm, "end": v(-53.45, 2.38) * mm});
            skLineSegment(sketch, "E48.1", {"start": v(-53.45, 2.38) * mm, "end": v(-53.45, -12.9) * mm});
            skLineSegment(sketch, "E48.2", {"start": v(-53.45, -12.9) * mm, "end": v(-66.67, -20.54) * mm});
            skLineSegment(sketch, "E48.3", {"start": v(-66.67, -20.54) * mm, "end": v(-79.9, -12.9) * mm});
            skLineSegment(sketch, "E48.4", {"start": v(-79.9, -12.9) * mm, "end": v(-79.9, 2.38) * mm});
            skLineSegment(sketch, "E48.5", {"start": v(-79.9, 2.38) * mm, "end": v(-66.67, 10.01) * mm});
            skPoint(sketch, "E48.0.midPoint", {"position": v(-60.06, 6.2) * mm});
            skCircle(sketch, "E49", {"center": v(-66.67, 10.01) * mm, "radius": 1.5 * mm});
            skCircle(sketch, "E50", {"center": v(-79.9, -12.9) * mm, "radius": 1.5 * mm});
            skCircle(sketch, "E51", {"center": v(-53.45, -12.9) * mm, "radius": 1.5 * mm});
            skCircle(sketch, "E52.cCircle", {"center": v(-66.67, -5.26) * mm, "radius": 8.88 * mm, "construction": true});
            skLineSegment(sketch, "E52.0", {"start": v(-57.8, -0.14) * mm, "end": v(-57.8, -10.39) * mm});
            skLineSegment(sketch, "E52.1", {"start": v(-57.8, -10.39) * mm, "end": v(-66.67, -15.5) * mm});
            skLineSegment(sketch, "E52.2", {"start": v(-66.67, -15.5) * mm, "end": v(-75.55, -10.39) * mm});
            skLineSegment(sketch, "E52.3", {"start": v(-75.55, -10.39) * mm, "end": v(-75.55, -0.14) * mm});
            skLineSegment(sketch, "E52.4", {"start": v(-75.55, -0.14) * mm, "end": v(-66.67, 4.99) * mm});
            skLineSegment(sketch, "E52.5", {"start": v(-66.67, 4.99) * mm, "end": v(-57.8, -0.14) * mm});
            skPoint(sketch, "E52.0.midPoint", {"position": v(-57.8, -5.26) * mm});
            skCircle(sketch, "E53", {"center": v(-66.67, -5.26) * mm, "radius": 7 * mm});
            skCircle(sketch, "E54.cCircle", {"center": v(-66.67, -5.26) * mm, "radius": 8.47 * mm, "construction": true});
            skLineSegment(sketch, "E54.0", {"start": v(-66.67, 4.52) * mm, "end": v(-58.2, -0.37) * mm});
            skLineSegment(sketch, "E54.1", {"start": v(-58.2, -0.37) * mm, "end": v(-58.2, -10.15) * mm});
            skLineSegment(sketch, "E54.2", {"start": v(-58.2, -10.15) * mm, "end": v(-66.67, -15.04) * mm});
            skLineSegment(sketch, "E54.3", {"start": v(-66.67, -15.04) * mm, "end": v(-75.14, -10.15) * mm});
            skLineSegment(sketch, "E54.4", {"start": v(-75.14, -10.15) * mm, "end": v(-75.14, -0.37) * mm});
            skLineSegment(sketch, "E54.5", {"start": v(-75.14, -0.37) * mm, "end": v(-66.67, 4.52) * mm});
            skPoint(sketch, "E54.0.midPoint", {"position": v(-62.44, 2.07) * mm});
            skCircle(sketch, "E55.cCircle", {"center": v(-66.67, -5.26) * mm, "radius": 9.12 * mm, "construction": true});
            skLineSegment(sketch, "E55.0", {"start": v(-66.67, 5.28) * mm, "end": v(-57.55, 0) * mm});
            skLineSegment(sketch, "E55.1", {"start": v(-57.55, 0) * mm, "end": v(-57.55, -10.53) * mm});
            skLineSegment(sketch, "E55.2", {"start": v(-57.55, -10.53) * mm, "end": v(-66.67, -15.8) * mm});
            skLineSegment(sketch, "E55.3", {"start": v(-66.67, -15.8) * mm, "end": v(-75.8, -10.53) * mm});
            skLineSegment(sketch, "E55.4", {"start": v(-75.8, -10.53) * mm, "end": v(-75.8, 0) * mm});
            skLineSegment(sketch, "E55.5", {"start": v(-75.8, 0) * mm, "end": v(-66.67, 5.28) * mm});
            skPoint(sketch, "E55.0.midPoint", {"position": v(-62.1, 2.64) * mm});
            skCircle(sketch, "E56", {"center": v(-66.67, -5.26) * mm, "radius": 17.27 * mm});
            skCircle(sketch, "E57", {"center": v(-66.67, -5.26) * mm, "radius": 17.5 * mm});
            skSolve(sketch);
        }
        {
            var Q0;
            Q0 = qSketchRegion(id + "F18", true);
            var Q1;
            Q1=makeQuery(id+"F18.imprint","IMPRINT",FACE,{"disambiguationData":[TD([[makeQuery(id+"F18.imprint","IMPRINT",EDGE,{"derivedFrom":sQuery(id+"F18.wireOp",EDGE,"E56")}),1.0]])]});
            var Q2;
            {var subQ0=sQuery(id+"F18.wireOp",EDGE,"E48.2");var subQ1=sQuery(id+"F18.wireOp",EDGE,"E48.1");var subQ2=makeQuery(id+"F18.imprint","INTERSECT",VERTEX,{"derivedFrom":[subQ1,subQ0]});Q2=makeQuery(id+"F18.imprint","IMPRINT",FACE,{"disambiguationData":[TD([[makeQuery(id+"F18.imprint","IMPRINT",EDGE,{"disambiguationData":[TD([[subQ2,1.0]])],"derivedFrom":subQ1}),1.0]])]});}
            var Q3;
            {var subQ0=sQuery(id+"F18.wireOp",EDGE,"E48.2");var subQ1=sQuery(id+"F18.wireOp",EDGE,"E48.1");var subQ2=makeQuery(id+"F18.imprint","INTERSECT",VERTEX,{"derivedFrom":[subQ1,subQ0]});Q3=makeQuery(id+"F18.imprint","IMPRINT",FACE,{"disambiguationData":[TD([[makeQuery(id+"F18.imprint","IMPRINT",EDGE,{"disambiguationData":[TD([[subQ2,1.0]])],"derivedFrom":subQ1}),-1.0]])]});}
            var Q4;
            {var subQ0=sQuery(id+"F18.wireOp",EDGE,"E48.4");var subQ1=sQuery(id+"F18.wireOp",EDGE,"E48.3");var subQ2=makeQuery(id+"F18.imprint","INTERSECT",VERTEX,{"derivedFrom":[subQ1,subQ0]});Q4=makeQuery(id+"F18.imprint","IMPRINT",FACE,{"disambiguationData":[TD([[makeQuery(id+"F18.imprint","IMPRINT",EDGE,{"disambiguationData":[TD([[subQ2,1.0]])],"derivedFrom":subQ1}),1.0]])]});}
            var Q5;
            {var subQ0=sQuery(id+"F18.wireOp",EDGE,"E48.4");var subQ1=sQuery(id+"F18.wireOp",EDGE,"E48.3");var subQ2=makeQuery(id+"F18.imprint","INTERSECT",VERTEX,{"derivedFrom":[subQ1,subQ0]});Q5=makeQuery(id+"F18.imprint","IMPRINT",FACE,{"disambiguationData":[TD([[makeQuery(id+"F18.imprint","IMPRINT",EDGE,{"disambiguationData":[TD([[subQ2,1.0]])],"derivedFrom":subQ1}),-1.0]])]});}
            var Q6;
            Q6=makeQuery(id+"F18.imprint","IMPRINT",FACE,{"disambiguationData":[TD([[makeQuery(id+"F18.imprint","IMPRINT",EDGE,{"derivedFrom":sQuery(id+"F18.wireOp",EDGE,"E55.0")}),1.0]])]});
            var Q7;
            {var subQ0=sQuery(id+"F18.wireOp",EDGE,"E48.5");var subQ1=sQuery(id+"F18.wireOp",EDGE,"E48.0");var subQ2=makeQuery(id+"F18.imprint","INTERSECT",VERTEX,{"derivedFrom":[subQ1,subQ0]});Q7=makeQuery(id+"F18.imprint","IMPRINT",FACE,{"disambiguationData":[TD([[makeQuery(id+"F18.imprint","IMPRINT",EDGE,{"disambiguationData":[TD([[subQ2,-1.0]])],"derivedFrom":subQ1}),-1.0]])]});}
            var Q8;
            {var subQ0=sQuery(id+"F18.wireOp",EDGE,"E48.5");var subQ1=sQuery(id+"F18.wireOp",EDGE,"E48.0");var subQ2=makeQuery(id+"F18.imprint","INTERSECT",VERTEX,{"derivedFrom":[subQ1,subQ0]});Q8=makeQuery(id+"F18.imprint","IMPRINT",FACE,{"disambiguationData":[TD([[makeQuery(id+"F18.imprint","IMPRINT",EDGE,{"disambiguationData":[TD([[subQ2,-1.0]])],"derivedFrom":subQ1}),1.0]])]});}
            extrude(context, id + "F19", {"entities" : qUnion([Q0, Q1, Q2, Q3, Q4, Q5, Q6, Q7, Q8]), "depth" : 3 * mm});
        }
    });
